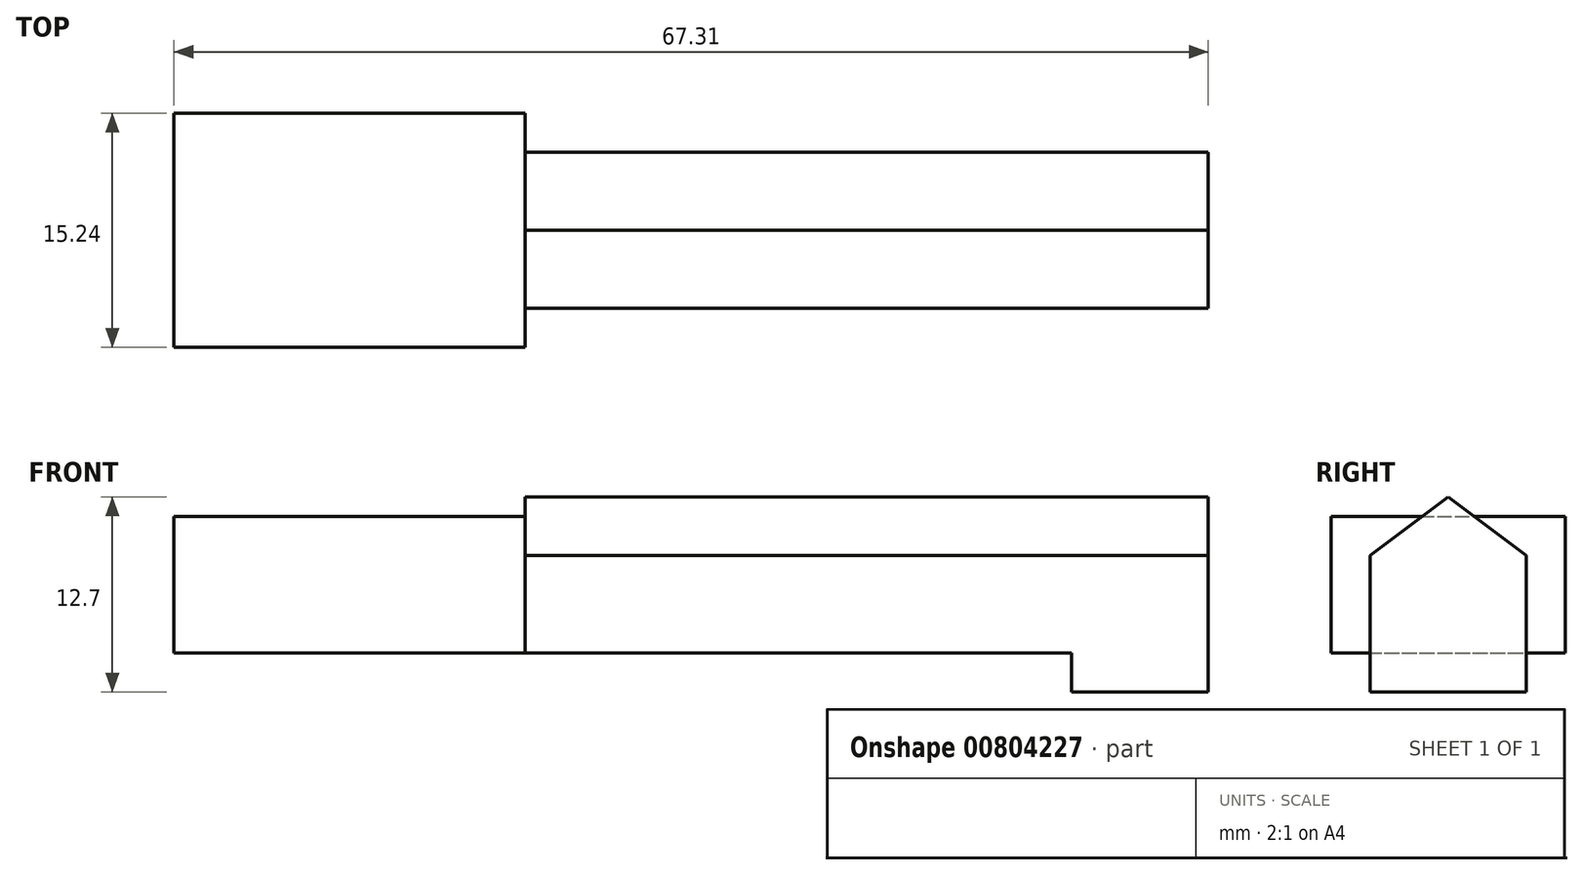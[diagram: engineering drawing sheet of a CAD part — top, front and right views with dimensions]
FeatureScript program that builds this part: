
annotation { "Feature Type Name" : "Feature", "Feature Type Description" : "" }
export const myFeature = defineFeature(function(context is Context, id is Id, definition is map)
    precondition{}
    {
        {
            var Q0;
            Q0=qCreatedBy(makeId("Front.planeOp"),FACE);
            var sketch = newSketch(context, id + "F0", { "sketchPlane" : qUnion([Q0])});
            skLineSegment(sketch, "E0", {"start": v(0, 0) * mm, "end": v(127, 0) * mm});
            skLineSegment(sketch, "E1", {"start": v(127, 0) * mm, "end": v(101.6, 0) * mm});
            skLineSegment(sketch, "E2", {"start": v(101.6, 0) * mm, "end": v(92.7, 0) * mm});
            skLineSegment(sketch, "E3", {"start": v(92.7, 0) * mm, "end": v(57.15, 0) * mm});
            skLineSegment(sketch, "E4", {"start": v(57.15, 0) * mm, "end": v(34.3, 0) * mm});
            skLineSegment(sketch, "E5", {"start": v(34.3, 0) * mm, "end": v(34.3, 8.89) * mm});
            skLineSegment(sketch, "E6", {"start": v(34.3, 8.89) * mm, "end": v(57.15, 8.89) * mm});
            skLineSegment(sketch, "E7", {"start": v(57.15, 8.89) * mm, "end": v(57.15, 0) * mm});
            skLineSegment(sketch, "E8", {"start": v(101.6, 0) * mm, "end": v(101.6, 10.16) * mm});
            skLineSegment(sketch, "E9", {"start": v(57.15, 0) * mm, "end": v(57.15, 10.16) * mm});
            skLineSegment(sketch, "E10", {"start": v(57.15, 10.16) * mm, "end": v(101.6, 10.16) * mm});
            skLineSegment(sketch, "E11", {"start": v(101.6, 0) * mm, "end": v(101.6, 6.35) * mm});
            skLineSegment(sketch, "E12", {"start": v(101.6, 6.35) * mm, "end": v(57.15, 6.35) * mm});
            skLineSegment(sketch, "E13", {"start": v(92.7, 0) * mm, "end": v(92.7, 6.35) * mm});
            skLineSegment(sketch, "E14", {"start": v(92.7, 6.35) * mm, "end": v(92.7, -2.54) * mm});
            skLineSegment(sketch, "E15", {"start": v(92.7, -2.54) * mm, "end": v(101.6, -2.54) * mm});
            skLineSegment(sketch, "E16", {"start": v(101.6, -2.54) * mm, "end": v(101.6, 0) * mm});
            skSolve(sketch);
        }
        {
            var Q0;
            {var subQ5=sQuery(id+"F0.wireOp",EDGE,"E5");Q0=makeQuery(id+"F0.imprint","IMPRINT",FACE,{"disambiguationData":[TD([[makeQuery(id+"F0.imprint","IMPRINT",EDGE,{"derivedFrom":subQ5}),-1.0]])]});}
            extrude(context, id + "F1", {"entities" : qUnion([Q0]), "depth" : 7.62 * mm, "offsetDistance" : 25.4 * mm});
        }
        {
            var Q0;
            {var subQ5=sQuery(id+"F0.wireOp",EDGE,"E5");Q0=makeQuery(id+"F0.imprint","IMPRINT",FACE,{"disambiguationData":[TD([[makeQuery(id+"F0.imprint","IMPRINT",EDGE,{"derivedFrom":subQ5}),-1.0]])]});}
            extrude(context, id + "F2", {"entities" : qUnion([Q0]), "operationType" : NewBodyOperationType.ADD, "depth" : -7.62 * mm, "offsetDistance" : 25.4 * mm});
        }
        {
            var Q0;
            {var subQ3=sQuery(id+"F0.wireOp",EDGE,"E13");Q0=makeQuery(id+"F0.imprint","IMPRINT",FACE,{"disambiguationData":[TD([[makeQuery(id+"F0.imprint","IMPRINT",EDGE,{"derivedFrom":subQ3}),1.0]])]});}
            var Q1;
            {var subQ3=sQuery(id+"F0.wireOp",EDGE,"E13");Q1=makeQuery(id+"F0.imprint","IMPRINT",FACE,{"disambiguationData":[TD([[makeQuery(id+"F0.imprint","IMPRINT",EDGE,{"derivedFrom":subQ3}),-1.0]])]});}
            var Q2;
            {var subQ2=sQuery(id+"F0.wireOp",EDGE,"E14");Q2=makeQuery(id+"F0.imprint","IMPRINT",FACE,{"disambiguationData":[TD([[makeQuery(id+"F0.imprint","IMPRINT",EDGE,{"derivedFrom":subQ2}),1.0]])]});}
            extrude(context, id + "F3", {"entities" : qUnion([Q0, Q1, Q2]), "operationType" : NewBodyOperationType.ADD, "depth" : 5.08 * mm, "offsetDistance" : 25.4 * mm});
        }
        {
            var Q0;
            {var subQ3=sQuery(id+"F0.wireOp",EDGE,"E13");Q0=makeQuery(id+"F0.imprint","IMPRINT",FACE,{"disambiguationData":[TD([[makeQuery(id+"F0.imprint","IMPRINT",EDGE,{"derivedFrom":subQ3}),1.0]])]});}
            var Q1;
            {var subQ3=sQuery(id+"F0.wireOp",EDGE,"E13");Q1=makeQuery(id+"F0.imprint","IMPRINT",FACE,{"disambiguationData":[TD([[makeQuery(id+"F0.imprint","IMPRINT",EDGE,{"derivedFrom":subQ3}),-1.0]])]});}
            var Q2;
            {var subQ2=sQuery(id+"F0.wireOp",EDGE,"E14");Q2=makeQuery(id+"F0.imprint","IMPRINT",FACE,{"disambiguationData":[TD([[makeQuery(id+"F0.imprint","IMPRINT",EDGE,{"derivedFrom":subQ2}),1.0]])]});}
            extrude(context, id + "F4", {"entities" : qUnion([Q0, Q1, Q2]), "operationType" : NewBodyOperationType.ADD, "depth" : -5.08 * mm, "offsetDistance" : 25.4 * mm});
        }
        {
            var Q0;
            {var subQ0=sQuery(id+"F0.wireOp",EDGE,"E16");var subQ1=sQuery(id+"F0.wireOp",EDGE,"E8");Q0=makeQuery(id+"F4.boolean.opBoolean","MERGE",FACE,{"derivedFrom":[makeQuery(id+"F3.opExtrude","SWEPT_FACE",FACE,{"disambiguationData":[OSD([subQ1,subQ0])]}),makeQuery(id+"F4.opExtrude","SWEPT_FACE",FACE,{"disambiguationData":[OSD([subQ1,subQ0])]})]});}
            var sketch = newSketch(context, id + "F5", { "sketchPlane" : qUnion([Q0])});
            skLineSegment(sketch, "E17", {"start": v(0, 6.35) * mm, "end": v(0, 10.16) * mm});
            skLineSegment(sketch, "E18", {"start": v(0, 10.16) * mm, "end": v(5.08, 6.35) * mm});
            skLineSegment(sketch, "E19", {"start": v(5.08, 6.35) * mm, "end": v(0, 10.16) * mm});
            skLineSegment(sketch, "E20", {"start": v(0, 10.16) * mm, "end": v(-5.08, 6.35) * mm});
            skSolve(sketch);
        }
        {
            var Q0;
            {var subQ0=sQuery(id+"F5.wireOp",EDGE,"E17");Q0=makeQuery(id+"F5.imprint","IMPRINT",FACE,{"disambiguationData":[TD([[makeQuery(id+"F5.imprint","IMPRINT",EDGE,{"derivedFrom":subQ0}),-1.0]])]});}
            var Q1;
            {var subQ0=sQuery(id+"F5.wireOp",EDGE,"E17");Q1=makeQuery(id+"F5.imprint","IMPRINT",FACE,{"disambiguationData":[TD([[makeQuery(id+"F5.imprint","IMPRINT",EDGE,{"derivedFrom":subQ0}),1.0]])]});}
            extrude(context, id + "F6", {"entities" : qUnion([Q0, Q1]), "operationType" : NewBodyOperationType.ADD, "depth" : -44.45 * mm, "offsetDistance" : 25.4 * mm});
        }
    });
